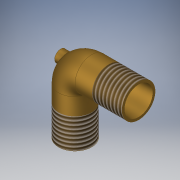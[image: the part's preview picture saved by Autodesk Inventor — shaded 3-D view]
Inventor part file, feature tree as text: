
AUTODESK INVENTOR PART (.ipt)
format: ipt  version: 2018 (Build 220112000, 112)  size: 791,040 bytes
history: native  units: in
note: dims shown in document units (in); Inventor stores cm internally (conversion verified against a paired STEP export)
features: sketch x7, extrude x6, other x3, plane x3, thread x2, chamfer x1
ambient origin geometry x8: Origin, YZ Plane, XZ Plane, XY Plane, X Axis, Y Axis, Z Axis, Center Point
bodies: Body1 (feature_tree)
feature tree (22):
  extrude  "Extrusion5"  Depth=0.5515in
  other  "Bend Part2"
  thread  "Thread3"  [1 undecoded]
  thread  "Thread4"  [1 undecoded]
  plane  "Work Plane3"
  extrude  "Extrusion6"  Depth=0.276in TaperAngle=90.0deg
  plane  "Work Plane4"
  extrude  "Extrusion7"  Depth=0.5in TaperAngle=0.0deg
  chamfer  "Chamfer2"  Distance=29.5276in Angle=360.0deg
  plane  "Work Plane5"
  extrude  "Extrusion8"  TaperAngle=0.0deg  [1 undecoded]
  extrude  "Extrusion9"  Depth=0.285in TaperAngle=45.0deg
  extrude  "Extrusion10"  TaperAngle=0.0deg  [1 undecoded]
  other  "Work Axis1"
  other  "Work Axis2"
  sketch  "Sketch6"  dims[d24=0.475in d25=0.5515in d26=2.0in d27=0.0in d28=2.0in]
  sketch  "Sketch7"  dims[d29=1.0in d30=0.276in d31=90.0deg]
  sketch  "Sketch8"  dims[d32=0.5in d33=0.0in d34=0.5in d35=0.0in]
  sketch  "Sketch9"  dims[d36=-0.45in]
  sketch  "Sketch10"  dims[d37=0.46in d38=29.5276in d40=360.0deg]
  sketch  "Sketch11"  dims[d42=0.45in d43=0.0in d44=0.0in]
  sketch  "Sketch12"  dims[d45=0.1in d46=0.0in d47=0.0925in d48=0.125in d49=45.0deg d50=0.0in d51=0.2in d52=0.3in d53=0.0in d54=0.075in d55=0.3in d56=0.0in d57=0.19in d58=0.285in d59=0.0in]
note: 4 required parameter values undecoded (feature->parameter linkage not recoverable at this tier; creation-order binding heuristic only, values carry confidence <= 0.55)
